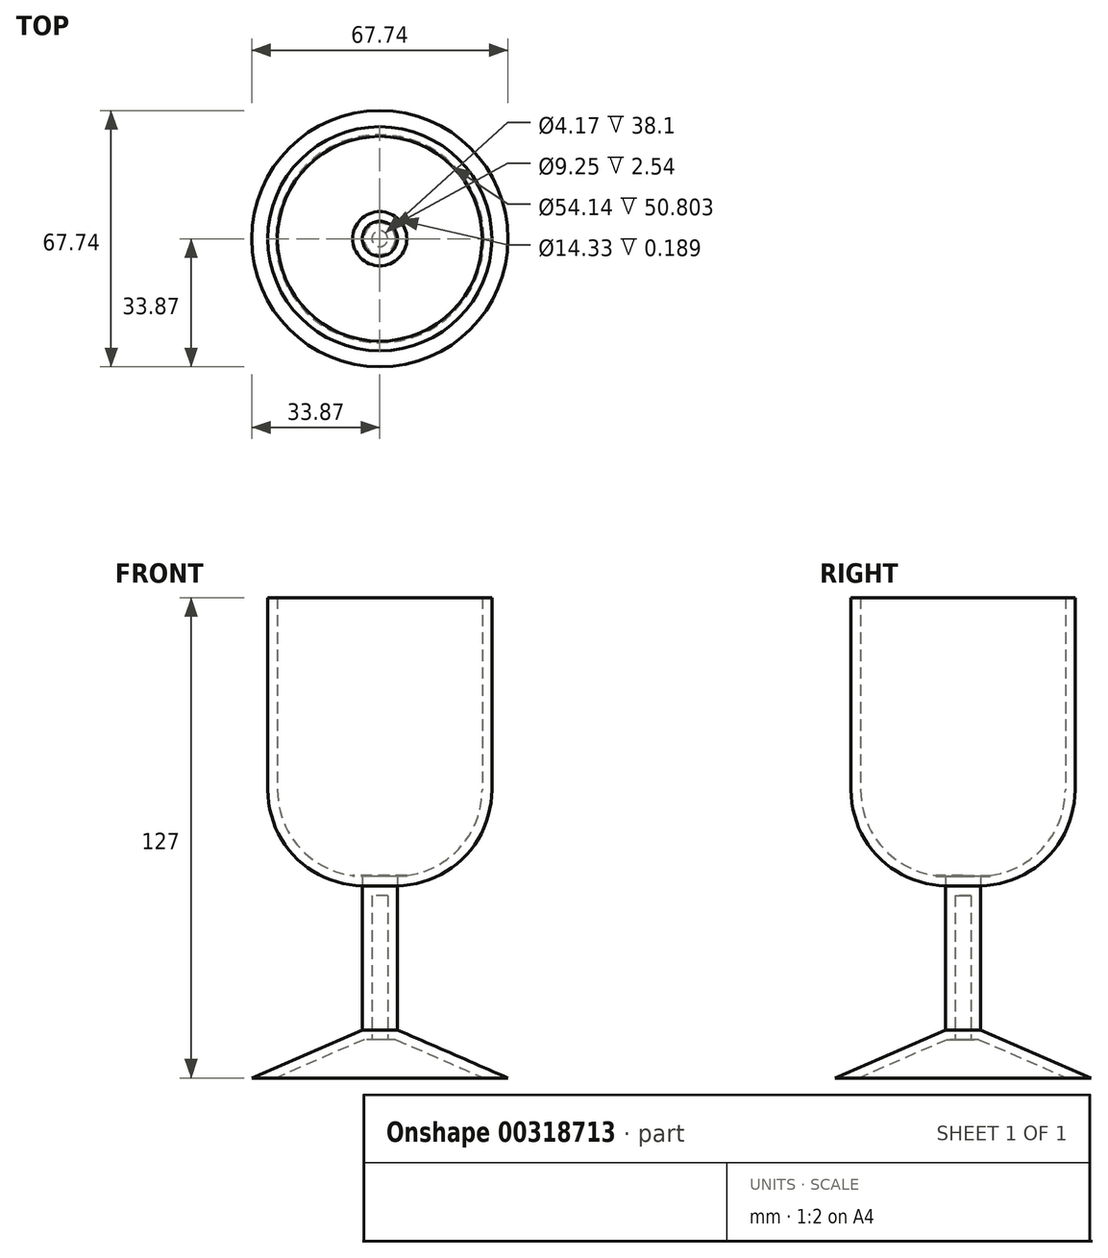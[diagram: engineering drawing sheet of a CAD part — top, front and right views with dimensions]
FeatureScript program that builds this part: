
annotation { "Feature Type Name" : "Feature", "Feature Type Description" : "" }
export const myFeature = defineFeature(function(context is Context, id is Id, definition is map)
    precondition{}
    {
        {
            var Q0;
            Q0=qCreatedBy(makeId("Top.planeOp"),FACE);
            var sketch = newSketch(context, id + "F0", { "sketchPlane" : qUnion([Q0])});
            skCircle(sketch, "E0", {"center": v(0, 0) * mm, "radius": 33.87 * mm});
            skSolve(sketch);
        }
        {
            var Q0;
            Q0=makeQuery(id+"F0.imprint","IMPRINT",FACE,{"disambiguationData":[TD([[makeQuery(id+"F0.imprint","IMPRINT",EDGE,{"derivedFrom":sQuery(id+"F0.wireOp",EDGE,"E0")}),1.0]])]});
            extrude(context, id + "F1", {"entities" : qUnion([Q0]), "depth" : 12.7 * mm});
        }
        {
            var Q0;
            Q0=makeQuery(id+"F1.opExtrude","CAP_EDGE",EDGE,{"disambiguationData":[OSD([sQuery(id+"F0.wireOp",EDGE,"E0")])],"isStart":false});
            chamfer(context, id + "F2", {"entities" : qUnion([Q0]), "chamferType" : ChamferType.TWO_OFFSETS, "width1" : 29.2 * mm, "oppositeDirection" : false, "width2" : 12.7 * mm, "tangentPropagation" : true});
        }
        {
            var Q0;
            Q0=makeQuery(id+"F1.opExtrude","CAP_FACE",FACE,{"disambiguationData":[OSD([sQuery(id+"F0.wireOp",EDGE,"E0")])],"isStart":false});
            var sketch = newSketch(context, id + "F3", { "sketchPlane" : qUnion([Q0])});
            skCircle(sketch, "E1", {"center": v(0, 0) * mm, "radius": 4.62 * mm});
            skSolve(sketch);
        }
        {
            var Q0;
            Q0=makeQuery(id+"F3.imprint","IMPRINT",FACE,{"disambiguationData":[TD([[makeQuery(id+"F3.imprint","IMPRINT",EDGE,{"derivedFrom":sQuery(id+"F3.wireOp",EDGE,"E1")}),1.0]])]});
            extrude(context, id + "F4", {"entities" : qUnion([Q0]), "operationType" : NewBodyOperationType.ADD, "depth" : 38.1 * mm});
        }
        {
            var Q0;
            Q0=makeQuery(id+"F4.opExtrude","CAP_FACE",FACE,{"disambiguationData":[OSD([sQuery(id+"F3.wireOp",EDGE,"E1")])],"isStart":false});
            var sketch = newSketch(context, id + "F5", { "sketchPlane" : qUnion([Q0])});
            skCircle(sketch, "E2", {"center": v(0, 0) * mm, "radius": 29.6 * mm});
            skSolve(sketch);
        }
        {
            var Q0;
            Q0=makeQuery(id+"F5.imprint","IMPRINT",FACE,{"disambiguationData":[TD([[makeQuery(id+"F5.imprint","IMPRINT",EDGE,{"derivedFrom":sQuery(id+"F5.wireOp",EDGE,"E2")}),1.0]])]});
            extrude(context, id + "F6", {"entities" : qUnion([Q0]), "depth" : 76.2 * mm});
        }
        {
            var Q0;
            Q0=makeQuery(id+"F6.opExtrude","CAP_EDGE",EDGE,{"disambiguationData":[OSD([sQuery(id+"F5.wireOp",EDGE,"E2")])],"isStart":true});
            fillet(context, id + "F7", {"entities" : qUnion([Q0]), "radius" : 25.4 * mm, "tangentPropagation" : true, "allowEdgeOverflow" : false});
        }
        {
            var Q0;
            Q0=makeQuery(id+"F6.opExtrude","CAP_FACE",FACE,{"disambiguationData":[OSD([sQuery(id+"F3.wireOp",EDGE,"E1"),sQuery(id+"F5.wireOp",EDGE,"E2")])],"isStart":false});
            shell(context, id + "F8", {"entities" : qUnion([Q0]), "thickness" : 2.54 * mm});
        }
        {
            var Q0;
            Q0=makeQuery(id+"F8.opShell","OFFSET_FACE",FACE,{"disambiguationData":[OSD([sQuery(id+"F3.wireOp",EDGE,"E1"),sQuery(id+"F5.wireOp",EDGE,"E2")])]});
            extrude(context, id + "F9", {"entities" : qUnion([Q0]), "operationType" : NewBodyOperationType.REMOVE, "oppositeDirection" : true, "depth" : 73.66 * mm});
        }
        {
            var Q0;
            Q0=makeQuery(id+"F1.opExtrude","CAP_FACE",FACE,{"disambiguationData":[OSD([sQuery(id+"F0.wireOp",EDGE,"E0")])],"isStart":true});
            shell(context, id + "F10", {"entities" : qUnion([Q0]), "thickness" : 2.54 * mm});
        }
    });
